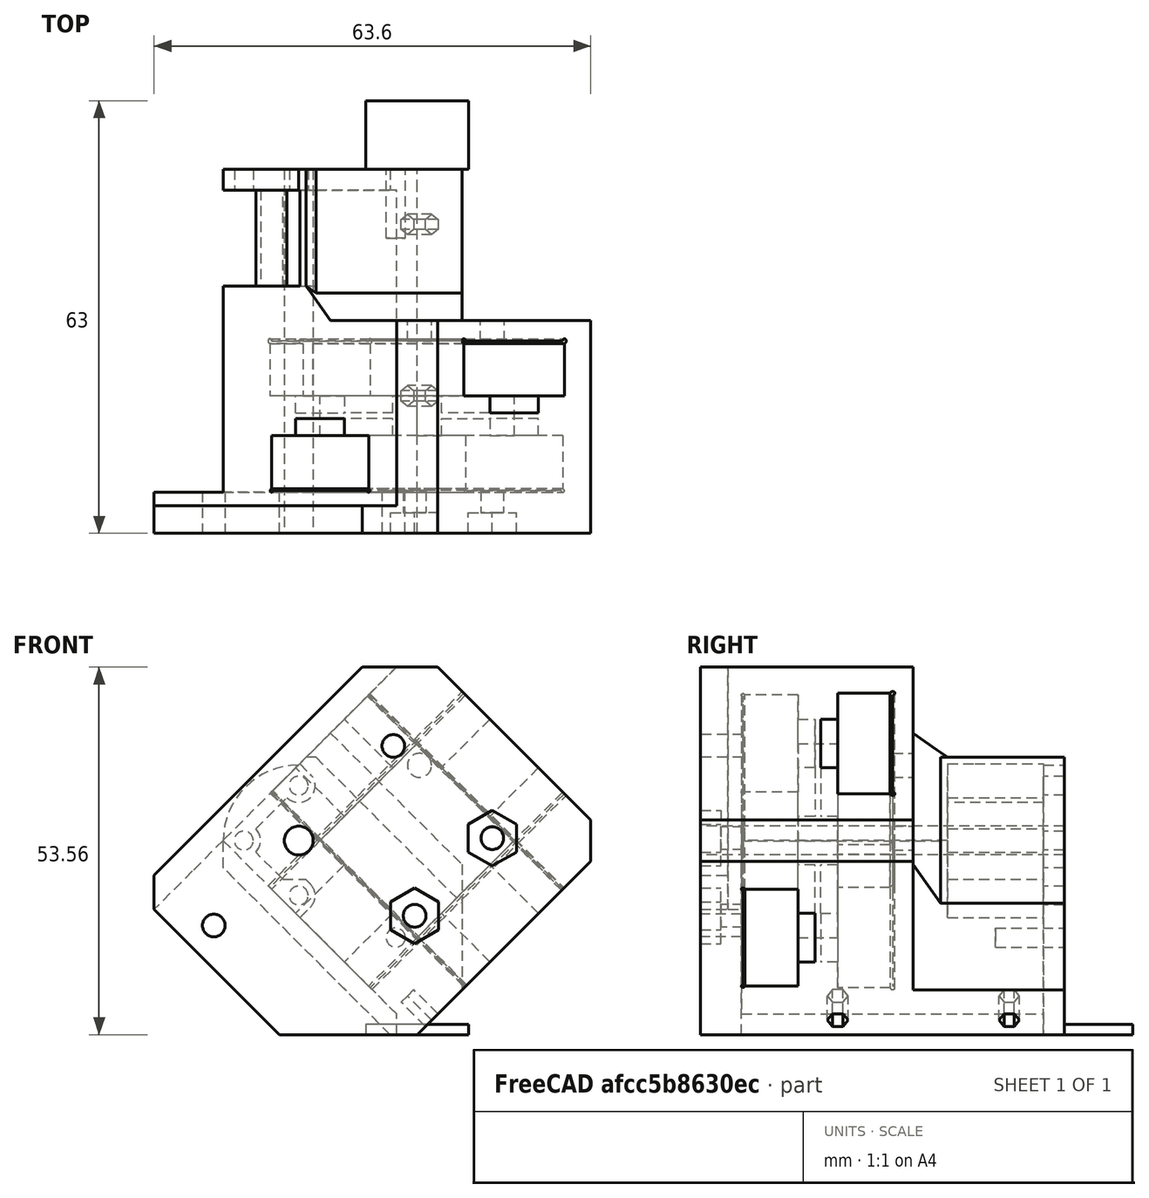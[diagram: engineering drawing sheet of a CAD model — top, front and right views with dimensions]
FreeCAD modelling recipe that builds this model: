
FCSTD DOCUMENT  (FreeCAD 0.19R)
Label: ToolHead_NoScreen
License: All rights reserved
LicenseURL: http://en.wikipedia.org/wiki/All_rights_reserved
objects: Sketcher::SketchObject×23, PartDesign::Pocket×14, PartDesign::Pad×5, PartDesign::Chamfer×2, PartDesign::Body×1
note: 66 computed .brp shape members not serialized (recipe doc carries the construction recipe); baked Part::Feature solids carry a one-line shape summary decoded from their .brp

FEATURE [Sketcher::SketchObject] Sketch  label="Body001"
  FullyConstrained = true
  MapMode = 5
  Support = -> [XY_Plane]
  sketch-geometry (11):
    g0: LineSegment StartX=20 StartY=15.7574 StartZ=0 EndX=20 EndY=-15.7574 EndZ=0
    g1: LineSegment StartX=15.7574 StartY=-20 StartZ=0 EndX=-20 EndY=-20 EndZ=0
    g2: LineSegment StartX=-20 StartY=-15.7574 StartZ=0 EndX=-20 EndY=19.9515 EndZ=0
    g3: Circle CenterX=-12.1976 CenterY=12.1976 CenterZ=0 NormalX=0 NormalY=0 NormalZ=1 AngleXU=0 Radius=2.1
    g4: LineSegment StartX=-12.1976 StartY=12.1976 StartZ=0 EndX=0 EndY=0 EndZ=0
    g5: ArcOfCircle CenterX=-12.1976 CenterY=12.1976 CenterZ=0 NormalX=0 NormalY=0 NormalZ=1 AngleXU=0 Radius=11 StartAngle=0.788519 EndAngle=2.35931
    g6: LineSegment StartX=-4.44373 StartY=20 StartZ=0 EndX=15.7574 EndY=20 EndZ=0
    g7: LineSegment StartX=15.7574 StartY=-20 StartZ=0 EndX=20 EndY=-15.7574 EndZ=0
    g8: LineSegment StartX=-20 StartY=-15.7574 StartZ=0 EndX=-22.1213 EndY=-17.8787 EndZ=0
    g9: LineSegment StartX=-22.1213 StartY=-17.8787 StartZ=0 EndX=-20 EndY=-20 EndZ=0
    g10: LineSegment StartX=15.7574 StartY=20 StartZ=0 EndX=20 EndY=15.7574 EndZ=0
  constraints (32):
    c: Horizontal(g1)
    c: Vertical(g0)
    c: Vertical(g2)
    c: Distance(g-1,g3) = 17.25
    c: Coincident(g4,g3)
    c: Coincident(g4,g-1)
    c: Angle(g4) = -0.785398
    c: Diameter(g3) = 4.2
    c: Coincident(g5,g3)
    c: Diameter(g5) = 22
    c: DistanceX(g1) = -20
    c: Coincident(g6,g5)
    c: Horizontal(g6)
    c: Coincident(g5,g2)
    c: Coincident(g7,g1)
    c: Coincident(g7,g0)
    c: Angle(g7) = 0.785398
    c: Distance(g7) = 6
    c: DistanceY(g1) = -20
    c: Coincident(g2,g8)
    c: Coincident(g8,g9)
    c: Coincident(g9,g1)
    c: Angle(g9) = -0.785398
    c: Angle(g8) = -2.35619
    c: Distance(g9) = 3
    c: DistanceX(g2) = -20
    c: Coincident(g10,g6)
    c: Coincident(g10,g0)
    c: Distance(g10) = 6
    c: Angle(g10) = -0.785398
    c: DistanceX(g0) = 20
    c: DistanceY(g6) = 20
FEATURE [PartDesign::Pad] Pad
  Direction = (1,1,1)
  Length = 53
  Length2 = 10
  Profile = -> Sketch
  Reversed = true
  Type = 0
FEATURE [Sketcher::SketchObject] Sketch001  label="RailHole"
  FullyConstrained = true
  MapMode = 5
  Placement = pos=(20,0,0) rot=(0.57735,0.57735,0.57735;2.0944rad)
  Support = -> [Pad]
  sketch-geometry (10):
    g0: LineSegment StartX=-10.35 StartY=-27.65 StartZ=0 EndX=-10.35 EndY=-20 EndZ=0
    g1: LineSegment StartX=5 StartY=-17.5 StartZ=0 EndX=-5 EndY=-17.5 EndZ=0
    g2: LineSegment StartX=10 StartY=-28 StartZ=0 EndX=-10 EndY=-28 EndZ=0
    g3: LineSegment StartX=5 StartY=-17.5 StartZ=0 EndX=5 EndY=-20 EndZ=0
    g4: LineSegment StartX=-5 StartY=-20 StartZ=0 EndX=-5 EndY=-17.5 EndZ=0
    g5: LineSegment StartX=-10.35 StartY=-20 StartZ=0 EndX=-5 EndY=-20 EndZ=0
    g6: LineSegment StartX=5 StartY=-20 StartZ=0 EndX=10.3495 EndY=-20 EndZ=0
    g7: LineSegment StartX=10.3495 StartY=-27.65 StartZ=0 EndX=10.3495 EndY=-20 EndZ=0
    g8: ArcOfCircle CenterX=-10.35 CenterY=-28 CenterZ=0 NormalX=0 NormalY=0 NormalZ=1 AngleXU=0 Radius=0.35 StartAngle=1.5708 EndAngle=6.28319
    g9: ArcOfCircle CenterX=10.35 CenterY=-28 CenterZ=0 NormalX=0 NormalY=0 NormalZ=1 AngleXU=0 Radius=0.35 StartAngle=3.14159 EndAngle=7.85541
  constraints (29):
    c: Vertical(g0)
    c: Symmetric(g1,g1,g-2)
    c: Distance(g1) = 10
    c: Coincident(g1,g3)
    c: Vertical(g3)
    c: Coincident(g4,g1)
    c: Symmetric(g3,g4,g-2)
    c: Distance(g3) = 2.5
    c: Distance(g2) = 20
    c: Coincident(g5,g4)
    c: Horizontal(g5)
    c: Coincident(g3,g6)
    c: Horizontal(g6)
    c: Vertical(g7)
    c: Coincident(g0,g5)
    c: Coincident(g7,g6)
    c: Coincident(g0,g8)
    c: Coincident(g8,g2)
    c: Diameter(g8) = 0.7
    c: DistanceX(g0,g8) = 0
    c: DistanceY(g2,g8) = 0
    c: Coincident(g9,g2)
    c: Coincident(g9,g7)
    c: Diameter(g9) = 0.7
    c: DistanceY(g2,g9) = 0
    c: DistanceX(g7,g9) = 0.0005
    c: Symmetric(g9,g8,g-2)
    c: Distance(g9,g6) = 8
    c: DistanceY(g8) = -28
FEATURE [PartDesign::Pocket] Pocket
  BaseFeature = -> Pad
  Length = 5
  Length2 = 100
  Profile = -> Sketch001
  Type = 1
FEATURE [Sketcher::SketchObject] Sketch008  label="ExtruderHole"
  FullyConstrained = false
  MapMode = 5
  Placement = pos=(0,0,4) rot=(0,0,1;0rad)
  sketch-geometry (2):
    g0: LineSegment StartX=0 StartY=0 StartZ=0 EndX=-54.6242 EndY=54.6242 EndZ=0
    g1: Circle CenterX=-12.1976 CenterY=12.1976 CenterZ=0 NormalX=0 NormalY=0 NormalZ=1 AngleXU=0 Radius=2.1
  constraints (5):
    c: Coincident(g0,g-1)
    c: Angle(g0) = 2.35619
    c: PointOnObject(g1,g0)
    c: Distance(g-1,g1) = 17.25
    c: Diameter(g1) = 4.2
FEATURE [Sketcher::SketchObject] Sketch009  label="reference"
  FullyConstrained = false
  MapMode = 5
  Placement = pos=(0,0,-25) rot=(1,0,0;3.14159rad)
  sketch-geometry (2):
    g0: Circle CenterX=-12.0208 CenterY=-12.0208 CenterZ=0 NormalX=0 NormalY=0 NormalZ=1 AngleXU=0 Radius=10
    g1: LineSegment StartX=0 StartY=0 StartZ=0 EndX=-27.7674 EndY=-27.7674 EndZ=0
  constraints (5):
    c: Diameter(g0) = 20
    c: Coincident(g1,g-1)
    c: Angle(g1) = -2.35619
    c: PointOnObject(g0,g1)
    c: Distance(g0,g1) = 17
FEATURE [Sketcher::SketchObject] Sketch010  label="reference2"
  FullyConstrained = false
  MapMode = 5
  Placement = pos=(0,0,-37) rot=(1,0,0;3.14159rad)
  sketch-geometry (2):
    g0: Circle CenterX=-12.1976 CenterY=-12.1976 CenterZ=0 NormalX=0 NormalY=0 NormalZ=1 AngleXU=0 Radius=8
    g1: LineSegment StartX=0 StartY=0 StartZ=0 EndX=-38.1566 EndY=-38.1566 EndZ=0
  constraints (5):
    c: Diameter(g0) = 16
    c: Coincident(g1,g-1)
    c: Angle(g1) = -2.35619
    c: Distance(g0,g1) = 17.25
    c: PointOnObject(g0,g1)
FEATURE [Sketcher::SketchObject] Sketch021  label="InternalTri"
  FullyConstrained = true
  MapMode = 5
  Placement = pos=(0,-3e-15,-12) rot=(0,0,1;0rad)
  sketch-geometry (4):
    g0: LineSegment StartX=-10 StartY=10 StartZ=0 EndX=10 EndY=10 EndZ=0
    g1: LineSegment StartX=10 StartY=10 StartZ=0 EndX=10 EndY=-10 EndZ=0
    g2: LineSegment StartX=10 StartY=-10 StartZ=0 EndX=-10 EndY=-10 EndZ=0
    g3: LineSegment StartX=-10 StartY=-10 StartZ=0 EndX=-10 EndY=10 EndZ=0
  constraints (11):
    c: Coincident(g0,g1)
    c: Coincident(g1,g2)
    c: Coincident(g2,g3)
    c: Coincident(g3,g0)
    c: Horizontal(g0)
    c: Horizontal(g2)
    c: Vertical(g1)
    c: Vertical(g3)
    c: Symmetric(g1,g0,g-1)
    c: Equal(g1,g0)
    c: Distance(g1) = 20
FEATURE [PartDesign::Pocket] Pocket002
  BaseFeature = -> Pocket
  Length = 10
  Length2 = 2
  Profile = -> Sketch021
  Type = 4
FEATURE [Sketcher::SketchObject] Sketch019  label="RailHole2"
  FullyConstrained = true
  MapMode = 5
  Placement = pos=(0,-20,0) rot=(1,0,0;1.5708rad)
  Support = -> [Pocket002]
  sketch-geometry (10):
    g0: LineSegment StartX=-9.75 StartY=-6.2 StartZ=0 EndX=9.75 EndY=-6.2 EndZ=0
    g1: LineSegment StartX=10 StartY=-14.2 StartZ=0 EndX=5 EndY=-14.2 EndZ=0
    g2: LineSegment StartX=5 StartY=-14.2 StartZ=0 EndX=5 EndY=-16.7 EndZ=0
    g3: LineSegment StartX=5 StartY=-16.7 StartZ=0 EndX=-5 EndY=-16.7 EndZ=0
    g4: LineSegment StartX=-5 StartY=-16.7 StartZ=0 EndX=-5 EndY=-14.2 EndZ=0
    g5: LineSegment StartX=-5 StartY=-14.2 StartZ=0 EndX=-10 EndY=-14.2 EndZ=0
    g6: ArcOfCircle CenterX=10 CenterY=-6.2 CenterZ=0 NormalX=0 NormalY=0 NormalZ=1 AngleXU=0 Radius=0.25 StartAngle=4.71239 EndAngle=9.42478
    g7: ArcOfCircle CenterX=-10 CenterY=-6.2 CenterZ=0 NormalX=0 NormalY=0 NormalZ=1 AngleXU=0 Radius=0.25 StartAngle=-9e-16 EndAngle=4.71239
    g8: LineSegment StartX=-10 StartY=-14.2 StartZ=0 EndX=-10 EndY=-6.45 EndZ=0
    g9: LineSegment StartX=10 StartY=-14.2 StartZ=0 EndX=10 EndY=-6.45 EndZ=0
  constraints (29):
    c: Horizontal(g0)
    c: Horizontal(g1)
    c: Coincident(g1,g2)
    c: Vertical(g2)
    c: Coincident(g2,g3)
    c: Horizontal(g3)
    c: Coincident(g3,g4)
    c: Vertical(g4)
    c: Coincident(g4,g5)
    c: Symmetric(g1,g5,g-2)
    c: Distance(g3) = 10
    c: Symmetric(g4,g1,g-2)
    c: DistanceY(g0) = -6.2
    c: Distance(g2) = 2.5
    c: Coincident(g6,g0)
    c: Coincident(g7,g0)
    c: Distance(g7,g6) = 20
    c: DistanceY(g1,g6) = 8
    c: Coincident(g8,g5)
    c: Vertical(g8)
    c: Coincident(g9,g1)
    c: Coincident(g9,g6)
    c: Vertical(g9)
    c: Coincident(g7,g8)
    c: Symmetric(g6,g7,g-2)
    c: Diameter(g6) = 0.5
    c: Equal(g6,g7)
    c: DistanceX(g7,g7) = 0
    c: DistanceY(g7,g0) = 0
FEATURE [Sketcher::SketchObject] Sketch024  label="hgxLITEholes"
  FullyConstrained = false
  MapMode = 5
  Placement = pos=(0,0,4) rot=(0,0,1;0rad)
  sketch-geometry (5):
    g0: Circle CenterX=7.30241 CenterY=12.1976 CenterZ=0 NormalX=0 NormalY=0 NormalZ=1 AngleXU=0 Radius=1.65
    g1: Circle CenterX=-29.6976 CenterY=12.1976 CenterZ=0 NormalX=0 NormalY=0 NormalZ=1 AngleXU=0 Radius=1.65
    g2: LineSegment StartX=-29.6976 StartY=12.1976 StartZ=0 EndX=7.30241 EndY=12.1976 EndZ=0
    g3: LineSegment StartX=0 StartY=0 StartZ=0 EndX=-27.1729 EndY=27.1729 EndZ=0
    g4: Circle CenterX=-12.1976 CenterY=12.1976 CenterZ=0 NormalX=0 NormalY=0 NormalZ=1 AngleXU=0 Radius=1.0154
  constraints (12):
    c: Diameter(g0) = 3.3
    c: Equal(g0,g1)
    c: Coincident(g2,g1)
    c: Coincident(g2,g0)
    c: Distance(g2) = 37
    c: Coincident(g3,g-1)
    c: Angle(g3) = 2.35619
    c: PointOnObject(g4,g3)
    c: Distance(g-1,g4) = 17.25
    c: Distance(g4,g0) = 19.5
    c: Horizontal(g2)
    c: PointOnObject(g4,g2)
FEATURE [PartDesign::Pocket] Pocket003
  BaseFeature = -> Pocket002
  Length = 5
  Length2 = 100
  Profile = -> Sketch019
  Type = 1
FEATURE [Sketcher::SketchObject] Sketch026  label="BottomSculp"
  FullyConstrained = false
  MapMode = 5
  Placement = pos=(0,0,-53) rot=(1,0,0;3.14159rad)
  Support = -> [Pocket003]
  sketch-geometry (5):
    g0: LineSegment StartX=29.4648 StartY=27.8981 StartZ=0 EndX=28.2209 EndY=-23.4245 EndZ=0
    g1: LineSegment StartX=28.2209 StartY=-23.4245 StartZ=0 EndX=-1.84855 EndY=-23.4245 EndZ=0
    g2: LineSegment StartX=-1.84855 StartY=-23.4245 StartZ=0 EndX=-1.84854 EndY=11.0762 EndZ=0
    g3: LineSegment StartX=-1.84854 StartY=11.0762 StartZ=0 EndX=-16.3575 EndY=25.5852 EndZ=0
    g4: LineSegment StartX=-16.3575 StartY=25.5852 StartZ=0 EndX=29.4648 EndY=27.8981 EndZ=0
  constraints (8):
    c: Coincident(g0,g1)
    c: Horizontal(g1)
    c: Coincident(g1,g2)
    c: Angle(g2) = 1.5708
    c: Coincident(g2,g3)
    c: Angle(g3) = 2.35619
    c: Coincident(g4,g3)
    c: Coincident(g4,g0)
FEATURE [PartDesign::Pocket] Pocket004
  BaseFeature = -> Pocket003
  Length = 22
  Length2 = 100
  Profile = -> Sketch026
  Type = 0
FEATURE [Sketcher::SketchObject] Sketch004  label="Yboltpattern"
  FullyConstrained = true
  MapMode = 5
  Placement = pos=(0,0,-31) rot=(1,0,0;3.14159rad)
  Support = -> [Pocket004]
  sketch-geometry (8):
    g0: Circle CenterX=-8 CenterY=7.5 CenterZ=0 NormalX=0 NormalY=0 NormalZ=1 AngleXU=0 Radius=1.75
    g1: Circle CenterX=8 CenterY=7.5 CenterZ=0 NormalX=0 NormalY=0 NormalZ=1 AngleXU=0 Radius=1.75
    g2: Circle CenterX=-8 CenterY=-7.5 CenterZ=0 NormalX=0 NormalY=0 NormalZ=1 AngleXU=0 Radius=1.75
    g3: Circle CenterX=8 CenterY=-7.5 CenterZ=0 NormalX=0 NormalY=0 NormalZ=1 AngleXU=0 Radius=1.75
    g4: LineSegment StartX=-8 StartY=7.5 StartZ=0 EndX=8 EndY=7.5 EndZ=0
    g5: LineSegment StartX=8 StartY=7.5 StartZ=0 EndX=8 EndY=-7.5 EndZ=0
    g6: LineSegment StartX=8 StartY=-7.5 StartZ=0 EndX=-8 EndY=-7.5 EndZ=0
    g7: LineSegment StartX=-8 StartY=-7.5 StartZ=0 EndX=-8 EndY=7.5 EndZ=0
  constraints (18):
    c: Diameter(g0) = 3.5
    c: Equal(g0,g1)
    c: Equal(g0,g2)
    c: Equal(g0,g3)
    c: Distance(g2,g0) = 15
    c: Distance(g3,g2) = 16
    c: Coincident(g4,g0)
    c: Coincident(g4,g1)
    c: Coincident(g4,g5)
    c: Coincident(g5,g3)
    c: Coincident(g5,g6)
    c: Coincident(g6,g2)
    c: Coincident(g6,g7)
    c: Coincident(g7,g4)
    c: Equal(g5,g7)
    c: Equal(g4,g6)
    c: Symmetric(g1,g2,g-1)
    c: Symmetric(g0,g1,g-2)
FEATURE [Sketcher::SketchObject] Sketch022  label="VoronHoleRelif"
  FullyConstrained = true
  MapMode = 5
  Placement = pos=(0,0,-28) rot=(0,0,1;0rad)
  Support = -> [Pocket004]
  sketch-geometry (11):
    g0: ArcOfCircle CenterX=-17.8884 CenterY=6.52425 CenterZ=0 NormalX=0 NormalY=0 NormalZ=1 AngleXU=0 Radius=2.4 StartAngle=4.71239 EndAngle=6.28319
    g1: ArcOfCircle CenterX=-6.58192 CenterY=17.8307 CenterZ=0 NormalX=0 NormalY=0 NormalZ=1 AngleXU=0 Radius=2.4 StartAngle=3.14159 EndAngle=6.28319
    g2: LineSegment StartX=-22.2684 StartY=4.12425 StartZ=0 EndX=-17.8884 EndY=4.12425 EndZ=0
    g3: LineSegment StartX=-22.2684 StartY=23.8307 StartZ=0 EndX=-4.18192 EndY=23.8307 EndZ=0
    g4: LineSegment StartX=-4.18192 StartY=23.8307 StartZ=0 EndX=-4.18192 EndY=17.8307 EndZ=0
    g5: LineSegment StartX=-22.2684 StartY=4.12425 StartZ=0 EndX=-22.2684 EndY=23.8307 EndZ=0
    g6: ArcOfCircle CenterX=-17.8172 CenterY=17.8307 CenterZ=0 NormalX=0 NormalY=0 NormalZ=1 AngleXU=0 Radius=2.4 StartAngle=4.71239 EndAngle=6.28319
    g7: LineSegment StartX=-15.4172 StartY=17.8307 StartZ=0 EndX=-8.98192 EndY=17.8307 EndZ=0
    g8: LineSegment StartX=-17.8172 StartY=9.85307 StartZ=0 EndX=-15.4884 EndY=7.52425 EndZ=0
    g9: LineSegment StartX=-15.4884 StartY=6.52425 StartZ=0 EndX=-15.4884 EndY=7.52425 EndZ=0
    g10: LineSegment StartX=-17.8172 StartY=9.85307 StartZ=0 EndX=-17.8172 EndY=15.4307 EndZ=0
  constraints (33):
    c: Horizontal(g2)
    c: Coincident(g3,g4)
    c: Tangent(g4,g1) = 1.5708
    c: Tangent(g2,g0) = -1.5708
    c: Diameter(g0) = 4.8
    c: Equal(g0,g1)
    c: Vertical(g4)
    c: Horizontal(g3)
    c: Coincident(g5,g2)
    c: Coincident(g5,g3)
    c: Vertical(g5)
    c: Distance(g2) = 4.38
    c: Distance(g4) = 6
    c: DistanceX(g1) = -6.58192
    c: DistanceY(g1) = 17.8307
    c: DistanceX(g0) = -17.8884
    c: DistanceY(g0) = 6.52425
    c: Coincident(g7,g6)
    c: Coincident(g7,g1)
    c: Horizontal(g7)
    c: Perpendicular(g1,g7)
    c: Diameter(g6) = 4.8
    c: Perpendicular(g6,g7)
    c: Angle(g8) = -0.785398
    c: Vertical(g9)
    c: Tangent(g9,g0) = -1.5708
    c: Distance(g9) = 1
    c: Coincident(g8,g9)
    c: Coincident(g10,g8)
    c: Coincident(g10,g6)
    c: Vertical(g10)
    c: Perpendicular(g6,g10)
    c: DistanceX(g6) = -17.8172
FEATURE [PartDesign::Pocket] Pocket005
  BaseFeature = -> Pocket004
  Length = 22
  Length2 = -8
  Profile = -> Sketch022
  Type = 4
FEATURE [Sketcher::SketchObject] Sketch017  label="VoronHoles3"
  FullyConstrained = true
  MapMode = 5
  Placement = pos=(0,0,-50) rot=(0,0,1;0rad)
  Support = -> [Pocket005]
  sketch-geometry (10):
    g0: Circle CenterX=-6.54074 CenterY=17.8544 CenterZ=0 NormalX=0 NormalY=0 NormalZ=1 AngleXU=0 Radius=1.375
    g1: Circle CenterX=-17.8544 CenterY=6.54074 CenterZ=0 NormalX=0 NormalY=0 NormalZ=1 AngleXU=0 Radius=1.375
    g2: Circle CenterX=-6.54074 CenterY=6.54074 CenterZ=0 NormalX=0 NormalY=0 NormalZ=1 AngleXU=0 Radius=1.375
    g3: Circle CenterX=-17.8544 CenterY=17.8544 CenterZ=0 NormalX=0 NormalY=0 NormalZ=1 AngleXU=0 Radius=1.375
    g4: LineSegment StartX=-6.54074 StartY=17.8544 StartZ=0 EndX=-6.54074 EndY=6.54074 EndZ=0
    g5: LineSegment StartX=-6.54074 StartY=6.54074 StartZ=0 EndX=-17.8544 EndY=6.54074 EndZ=0
    g6: LineSegment StartX=-17.8544 StartY=6.54074 StartZ=0 EndX=-17.8544 EndY=17.8544 EndZ=0
    g7: LineSegment StartX=-17.8544 StartY=17.8544 StartZ=0 EndX=-6.54074 EndY=17.8544 EndZ=0
    g8: LineSegment StartX=0 StartY=0 StartZ=0 EndX=-37.1726 EndY=37.1726 EndZ=0
    g9: Circle CenterX=-12.1976 CenterY=12.1976 CenterZ=0 NormalX=0 NormalY=0 NormalZ=1 AngleXU=0 Radius=0.77
  constraints (25):
    c: Coincident(g4,g0)
    c: Coincident(g4,g2)
    c: Coincident(g4,g5)
    c: Coincident(g5,g1)
    c: Coincident(g5,g6)
    c: Coincident(g6,g3)
    c: Coincident(g6,g7)
    c: Coincident(g7,g4)
    c: Equal(g4,g7)
    c: Equal(g7,g6)
    c: Equal(g6,g5)
    c: Coincident(g8,g-1)
    c: PointOnObject(g9,g8)
    c: Distance(g-1,g9) = 17.25
    c: Diameter(g1) = 2.75
    c: Equal(g1,g3)
    c: Equal(g1,g0)
    c: Equal(g1,g2)
    c: Symmetric(g0,g1,g9)
    c: Distance(g2,g3) = 16
    c: Angle(g8) = 2.35619
    c: PointOnObject(g2,g8)
    c: Perpendicular(g7,g4)
    c: Distance(g8) = 52.57
    c: Diameter(g9) = 1.54
FEATURE [PartDesign::Pocket] Pocket006
  BaseFeature = -> Pocket005
  Length = 5
  Length2 = 100
  Profile = -> Sketch017
  Type = 1
FEATURE [Sketcher::SketchObject] Sketch025  label="FanDuctMountHole"
  FullyConstrained = true
  MapMode = 5
  Placement = pos=(0,0,-53) rot=(1,0,0;3.14159rad)
  Support = -> [Pocket006]
  sketch-geometry (1):
    g0: Circle CenterX=-12.2 CenterY=7.8 CenterZ=0 NormalX=0 NormalY=0 NormalZ=1 AngleXU=0 Radius=1.4
  constraints (3):
    c: Diameter(g0) = 2.8
    c: DistanceX(g0) = -12.2
    c: DistanceY(g0) = 7.8
FEATURE [PartDesign::Pocket] Pocket007
  BaseFeature = -> Pocket006
  Length = 10
  Length2 = 100
  Profile = -> Sketch025
  Type = 0
FEATURE [PartDesign::Pocket] Pocket008
  BaseFeature = -> Pocket007
  Length = 9
  Length2 = 100
  Profile = -> Sketch004
  Type = 0
FEATURE [Sketcher::SketchObject] Sketch007  label="ExtruderPlatform"
  ExternalGeometry = -> [Pad]
  FullyConstrained = false
  MapMode = 5
  Support = -> [Pocket008]
  sketch-geometry (12):
    g0: LineSegment StartX=-20 StartY=-20 StartZ=0 EndX=15.7574 EndY=-20 EndZ=0
    g1: LineSegment StartX=0 StartY=0 StartZ=0 EndX=-70.7107 EndY=70.7107 EndZ=0
    g2: Circle CenterX=-12.1976 CenterY=12.1976 CenterZ=0 NormalX=0 NormalY=0 NormalZ=1 AngleXU=0 Radius=2.125
    g3: LineSegment StartX=15.7574 StartY=-20 StartZ=0 EndX=20 EndY=-15.7574 EndZ=0
    g4: LineSegment StartX=20 StartY=-15.7574 StartZ=0 EndX=20 EndY=15.7574 EndZ=0
    g5: LineSegment StartX=20 StartY=15.7574 StartZ=0 EndX=15.7574 EndY=20 EndZ=0
    g6: LineSegment StartX=-20 StartY=-20 StartZ=0 EndX=-34.1976 EndY=-5.80241 EndZ=0
    g7: LineSegment StartX=-12.1976 StartY=-100 StartZ=0 EndX=-12.1976 EndY=100 EndZ=0
    g8: LineSegment StartX=-34.1976 StartY=-5.80241 StartZ=0 EndX=-34.1976 EndY=20 EndZ=0
    g9: LineSegment StartX=-34.1976 StartY=20 StartZ=0 EndX=15.7574 EndY=20 EndZ=0
    g10: Circle CenterX=-29.6976 CenterY=12.1976 CenterZ=0 NormalX=0 NormalY=0 NormalZ=1 AngleXU=0 Radius=1.4
    g11: Circle CenterX=7.30241 CenterY=11.9057 CenterZ=0 NormalX=0 NormalY=0 NormalZ=1 AngleXU=0 Radius=1.4
  constraints (35):
    c: Coincident(g1,g-1)
    c: Angle(g1) = 2.35619
    c: Diameter(g2) = 4.25
    c: PointOnObject(g2,g1)
    c: Distance(g-1,g2) = 17.25
    c: Coincident(g0,g3)
    c: Coincident(g3,g4)
    c: Coincident(g6,g0)
    c: Angle(g6) = 2.35619
    c: Coincident(g5,g4)
    c: Distance(g1) = 100
    c: PointOnObject(g2,g7)
    c: DistanceX(g0,g0) = -35.7574
    c: DistanceY(g0,g0) = 0
    c: DistanceX(g3,g0) = -40
    c: DistanceY(g3,g0) = -4.24264
    c: DistanceX(g4) = 20
    c: DistanceY(g4) = 15.7574
    c: DistanceX(g3) = 20
    c: DistanceY(g3) = -15.7574
    c: Coincident(g8,g6)
    c: Vertical(g8)
    c: Horizontal(g9)
    c: Coincident(g5,g9)
    c: Distance(g8,g7) = 22
    c: DistanceX(g5) = 15.7574
    c: DistanceY(g5) = 20
    c: Symmetric(g7,g7,g-1)
    c: Distance(g7) = 200
    c: DistanceX(g10,g2) = 17.5
    c: DistanceX(g2,g11) = 19.5
    c: Diameter(g10) = 2.8
    c: Equal(g10,g11)
    c: DistanceY(g10,g2) = 0
    c: Coincident(g9,g8)
FEATURE [PartDesign::Pad] Pad001
  BaseFeature = -> Pocket008
  Direction = (1,1,1)
  Length = 6
  Length2 = 100
  Profile = -> Sketch007
  Reversed = true
  Type = 0
FEATURE [PartDesign::Pocket] Pocket009
  BaseFeature = -> Pad001
  Length = 11
  Length2 = 100
  Profile = -> Sketch024
  Type = 0
FEATURE [PartDesign::Pocket] Pocket010
  BaseFeature = -> Pocket009
  Length = 5
  Length2 = 100
  Profile = -> Sketch008
  Type = 1
FEATURE [Sketcher::SketchObject] Sketch003  label="Xboltpattern"
  FullyConstrained = true
  MapMode = 5
  Support = -> [Pocket010]
  sketch-geometry (8):
    g0: Circle CenterX=-8 CenterY=7.5 CenterZ=0 NormalX=0 NormalY=0 NormalZ=1 AngleXU=0 Radius=1.65
    g1: Circle CenterX=8 CenterY=7.5 CenterZ=0 NormalX=0 NormalY=0 NormalZ=1 AngleXU=0 Radius=1.65
    g2: Circle CenterX=-8 CenterY=-7.5 CenterZ=0 NormalX=0 NormalY=0 NormalZ=1 AngleXU=0 Radius=1.65
    g3: Circle CenterX=8 CenterY=-7.5 CenterZ=0 NormalX=0 NormalY=0 NormalZ=1 AngleXU=0 Radius=1.65
    g4: LineSegment StartX=-8 StartY=7.5 StartZ=0 EndX=8 EndY=7.5 EndZ=0
    g5: LineSegment StartX=8 StartY=7.5 StartZ=0 EndX=8 EndY=-7.5 EndZ=0
    g6: LineSegment StartX=8 StartY=-7.5 StartZ=0 EndX=-8 EndY=-7.5 EndZ=0
    g7: LineSegment StartX=-8 StartY=-7.5 StartZ=0 EndX=-8 EndY=7.5 EndZ=0
  constraints (19):
    c: Diameter(g0) = 3.3
    c: Equal(g0,g1)
    c: Equal(g0,g2)
    c: Equal(g0,g3)
    c: Distance(g0,g1) = 16
    c: Distance(g1,g3) = 15
    c: Coincident(g4,g0)
    c: Coincident(g4,g1)
    c: Horizontal(g4)
    c: Coincident(g4,g5)
    c: Coincident(g5,g3)
    c: Vertical(g5)
    c: Coincident(g5,g6)
    c: Coincident(g6,g2)
    c: Coincident(g6,g7)
    c: Coincident(g7,g4)
    c: Symmetric(g2,g1,g-1)
    c: Equal(g7,g5)
    c: Equal(g6,g4)
FEATURE [Sketcher::SketchObject] Sketch029  label="Adhesion"
  FullyConstrained = false
  MapMode = 5
  Placement = pos=(0,0,-53) rot=(1,0,0;3.14159rad)
  sketch-geometry (4):
    g0: LineSegment StartX=-13.636 StartY=24.2426 StartZ=0 EndX=-24.2426 EndY=13.636 EndZ=0
    g1: LineSegment StartX=-24.2426 StartY=13.636 StartZ=0 EndX=-25.3033 EndY=14.6967 EndZ=0
    g2: LineSegment StartX=-25.3033 StartY=14.6967 StartZ=0 EndX=-14.6967 EndY=25.3033 EndZ=0
    g3: LineSegment StartX=-14.6967 StartY=25.3033 StartZ=0 EndX=-13.636 EndY=24.2426 EndZ=0
  constraints (10):
    c: Coincident(g0,g1)
    c: Coincident(g1,g2)
    c: Coincident(g2,g3)
    c: Coincident(g3,g0)
    c: Angle(g2) = 0.785398
    c: Distance(g2) = 15
    c: Distance(g1) = 1.5
    c: Distance(g3) = 1.5
    c: Perpendicular(g2,g3)
    c: Perpendicular(g2,g1)
FEATURE [Sketcher::SketchObject] Sketch033  label="WireMgmnt"
  FullyConstrained = true
  MapMode = 5
  Placement = pos=(0,-20,0) rot=(1,0,0;1.5708rad)
  sketch-geometry (14):
    g0: LineSegment StartX=-15.7 StartY=-20.7506 StartZ=0 EndX=-15.7 EndY=-19.2494 EndZ=0
    g1: LineSegment StartX=-15.7 StartY=-19.2494 StartZ=0 EndX=-17 EndY=-18.4989 EndZ=0
    g2: LineSegment StartX=-17 StartY=-18.4989 StartZ=0 EndX=-18.3 EndY=-19.2494 EndZ=0
    g3: LineSegment StartX=-18.3 StartY=-19.2494 StartZ=0 EndX=-18.3 EndY=-20.7506 EndZ=0
    g4: LineSegment StartX=-18.3 StartY=-20.7506 StartZ=0 EndX=-17 EndY=-21.5011 EndZ=0
    g5: LineSegment StartX=-17 StartY=-21.5011 StartZ=0 EndX=-15.7 EndY=-20.7506 EndZ=0
    g6: Circle CenterX=-17 CenterY=-20 CenterZ=0 NormalX=0 NormalY=0 NormalZ=1 AngleXU=0 Radius=1.50111
    g7: LineSegment StartX=-15.7 StartY=-44.2494 StartZ=0 EndX=-17 EndY=-43.4989 EndZ=0
    g8: LineSegment StartX=-17 StartY=-43.4989 StartZ=0 EndX=-18.3 EndY=-44.2494 EndZ=0
    g9: LineSegment StartX=-18.3 StartY=-44.2494 StartZ=0 EndX=-18.3 EndY=-45.7506 EndZ=0
    g10: LineSegment StartX=-18.3 StartY=-45.7506 StartZ=0 EndX=-17 EndY=-46.5011 EndZ=0
    g11: LineSegment StartX=-17 StartY=-46.5011 StartZ=0 EndX=-15.7 EndY=-45.7506 EndZ=0
    g12: LineSegment StartX=-15.7 StartY=-45.7506 StartZ=0 EndX=-15.7 EndY=-44.2494 EndZ=0
    g13: Circle CenterX=-17 CenterY=-45 CenterZ=0 NormalX=0 NormalY=0 NormalZ=1 AngleXU=0 Radius=1.50111
  constraints (34):
    c: Coincident(g0,g1)
    c: Coincident(g1,g2)
    c: Coincident(g2,g3)
    c: Coincident(g3,g4)
    c: Coincident(g4,g5)
    c: Coincident(g5,g0)
    c: Equal(g0, g1-g5) x5
    c: PointOnObject(g0,g6)
    c: PointOnObject(g1,g6)
    c: PointOnObject(g2,g6)
    c: PointOnObject(g3,g6)
    c: PointOnObject(g4,g6)
    c: PointOnObject(g5,g6)
    c: Coincident(g7,g8)
    c: Coincident(g8,g9)
    c: Coincident(g9,g10)
    c: Coincident(g10,g11)
    c: Coincident(g11,g12)
    c: Coincident(g12,g7)
    c: Equal(g7, g8-g12) x5
    c: PointOnObject(g7,g13)
    c: PointOnObject(g8,g13)
    c: PointOnObject(g9,g13)
    c: PointOnObject(g10,g13)
    c: PointOnObject(g11,g13)
    c: PointOnObject(g12,g13)
    c: DistanceX(g13) = -17
    c: Distance(g10,g7) = 2.6
    c: Vertical(g9)
    c: DistanceY(g13) = -45
    c: Distance(g3,g0) = 2.6
    c: DistanceY(g6) = -20
    c: Vertical(g3)
    c: DistanceX(g6) = -17
FEATURE [Sketcher::SketchObject] Sketch035  label="Bottom Reinforce"
  FullyConstrained = false
  MapMode = 5
  Placement = pos=(0,0,-53) rot=(1,0,0;3.14159rad)
  sketch-geometry (4):
    g0: LineSegment StartX=-22.779 StartY=17.221 StartZ=0 EndX=-22.779 EndY=-17.1725 EndZ=0
    g1: LineSegment StartX=-22.779 StartY=-17.1725 StartZ=0 EndX=-20 EndY=-19.9515 EndZ=0
    g2: LineSegment StartX=-20 StartY=-19.9515 StartZ=0 EndX=-20 EndY=20 EndZ=0
    g3: LineSegment StartX=-20 StartY=20 StartZ=0 EndX=-22.779 EndY=17.221 EndZ=0
  constraints (9):
    c: Vertical(g0)
    c: Coincident(g0,g1)
    c: Coincident(g1,g2)
    c: Vertical(g2)
    c: Coincident(g2,g3)
    c: Coincident(g3,g0)
    c: Angle(g1) = -0.785398
    c: DistanceY(g2) = 20
    c: Angle(g3) = -2.35619
FEATURE [Sketcher::SketchObject] Sketch037
  FullyConstrained = false
  MapMode = 5
  sketch-geometry (4):
    g0: LineSegment StartX=-26.2848 StartY=31.2083 StartZ=0 EndX=-1.26106 EndY=31.2083 EndZ=0
    g1: LineSegment StartX=-1.26106 StartY=31.2083 StartZ=0 EndX=-1.26106 EndY=20 EndZ=0
    g2: LineSegment StartX=-1.26106 StartY=20 StartZ=0 EndX=-26.2848 EndY=20 EndZ=0
    g3: LineSegment StartX=-26.2848 StartY=20 StartZ=0 EndX=-26.2848 EndY=31.2083 EndZ=0
  constraints (9):
    c: Coincident(g0,g1)
    c: Coincident(g1,g2)
    c: Coincident(g2,g3)
    c: Coincident(g3,g0)
    c: Horizontal(g0)
    c: Horizontal(g2)
    c: Vertical(g1)
    c: Vertical(g3)
    c: DistanceY(g1) = 20
FEATURE [PartDesign::Pocket] Pocket011
  BaseFeature = -> Pocket010
  Length = 10
  Length2 = 100
  Profile = -> Sketch003
  Type = 0
FEATURE [Sketcher::SketchObject] Sketch036  label="countersink"
  FullyConstrained = true
  MapMode = 5
  Support = -> [Pocket011]
  sketch-geometry (14):
    g0: LineSegment StartX=11.9037 StartY=-8.546 StartZ=0 EndX=10.8577 EndY=-4.64226 EndZ=0
    g1: LineSegment StartX=10.8577 StartY=-4.64226 StartZ=0 EndX=6.954 EndY=-3.59626 EndZ=0
    g2: LineSegment StartX=6.954 StartY=-3.59626 StartZ=0 EndX=4.09626 EndY=-6.454 EndZ=0
    g3: LineSegment StartX=4.09626 StartY=-6.454 StartZ=0 EndX=5.14226 EndY=-10.3577 EndZ=0
    g4: LineSegment StartX=5.14226 StartY=-10.3577 StartZ=0 EndX=9.046 EndY=-11.4037 EndZ=0
    g5: LineSegment StartX=9.046 StartY=-11.4037 StartZ=0 EndX=11.9037 EndY=-8.546 EndZ=0
    g6: Circle CenterX=8 CenterY=-7.5 CenterZ=0 NormalX=0 NormalY=0 NormalZ=1 AngleXU=0 Radius=4.04145
    g7: LineSegment StartX=-5.14226 StartY=-4.64226 StartZ=0 EndX=-9.046 EndY=-3.59626 EndZ=0
    g8: LineSegment StartX=-9.046 StartY=-3.59626 StartZ=0 EndX=-11.9037 EndY=-6.454 EndZ=0
    g9: LineSegment StartX=-11.9037 StartY=-6.454 StartZ=0 EndX=-10.8577 EndY=-10.3577 EndZ=0
    g10: LineSegment StartX=-10.8577 StartY=-10.3577 StartZ=0 EndX=-6.954 EndY=-11.4037 EndZ=0
    g11: LineSegment StartX=-6.954 StartY=-11.4037 StartZ=0 EndX=-4.09626 EndY=-8.546 EndZ=0
    g12: LineSegment StartX=-4.09626 StartY=-8.546 StartZ=0 EndX=-5.14226 EndY=-4.64226 EndZ=0
    g13: Circle CenterX=-8 CenterY=-7.5 CenterZ=0 NormalX=0 NormalY=0 NormalZ=1 AngleXU=0 Radius=4.04145
  constraints (34):
    c: Coincident(g0,g1)
    c: Coincident(g1,g2)
    c: Coincident(g2,g3)
    c: Coincident(g3,g4)
    c: Coincident(g4,g5)
    c: Coincident(g5,g0)
    c: Equal(g0, g1-g5) x5
    c: PointOnObject(g0,g6)
    c: PointOnObject(g1,g6)
    c: PointOnObject(g2,g6)
    c: PointOnObject(g3,g6)
    c: PointOnObject(g4,g6)
    c: PointOnObject(g5,g6)
    c: Coincident(g7,g8)
    c: Coincident(g8,g9)
    c: Coincident(g9,g10)
    c: Coincident(g10,g11)
    c: Coincident(g11,g12)
    c: Coincident(g12,g7)
    c: Equal(g7, g8-g12) x5
    c: PointOnObject(g7,g13)
    c: PointOnObject(g8,g13)
    c: PointOnObject(g9,g13)
    c: PointOnObject(g10,g13)
    c: PointOnObject(g11,g13)
    c: PointOnObject(g12,g13)
    c: Angle(g11) = 0.785398
    c: Angle(g5) = 0.785398
    c: Distance(g0,g2) = 7
    c: Distance(g7,g8) = 7
    c: DistanceX(g6) = 8
    c: DistanceY(g6) = -7.5
    c: DistanceY(g13) = -7.5
    c: DistanceX(g13) = -8
FEATURE [PartDesign::Pocket] Pocket012
  BaseFeature = -> Pocket011
  Length = 3
  Length2 = 100
  Profile = -> Sketch036
  Type = 0
FEATURE [PartDesign::Pocket] Pocket013
  BaseFeature = -> Pocket012
  Length = 5
  Length2 = 100
  Profile = -> Sketch033
  Type = 0
FEATURE [PartDesign::Pad] Pad002
  BaseFeature = -> Pocket013
  Direction = (1,1,1)
  Length = 3
  Length2 = 100
  Profile = -> Sketch035
  Reversed = true
  Type = 0
FEATURE [PartDesign::Pocket] Pocket014
  BaseFeature = -> Pad002
  Length = 40
  Length2 = 100
  Profile = -> Sketch037
  Type = 0
FEATURE [PartDesign::Pad] Pad003
  BaseFeature = -> Pocket014
  Direction = (1,1,1)
  Length = 10
  Length2 = 100
  Profile = -> Sketch029
  Type = 0
FEATURE [Sketcher::SketchObject] Sketch038
  FullyConstrained = true
  MapMode = 5
  Placement = pos=(0,20,0) rot=(0,0.707107,0.707107;3.14159rad)
  Support = -> [Pad003]
FEATURE [Sketcher::SketchObject] Sketch039
  ExternalGeometry = -> [Pad003]
  FullyConstrained = true
  MapMode = 5
  Support = -> [Pad003]
  sketch-geometry (4):
    g0: LineSegment StartX=-30.6621 StartY=23.5355 StartZ=0 EndX=12.2218 EndY=23.5355 EndZ=0
    g1: LineSegment StartX=12.2218 StartY=23.5355 StartZ=0 EndX=15.7574 EndY=20 EndZ=0
    g2: LineSegment StartX=15.7574 StartY=20 StartZ=0 EndX=-34.1976 EndY=20 EndZ=0
    g3: LineSegment StartX=-34.1976 StartY=20 StartZ=0 EndX=-30.6621 EndY=23.5355 EndZ=0
  constraints (10):
    c: Coincident(g0,g1)
    c: Coincident(g1,g2)
    c: Coincident(g2,g3)
    c: Coincident(g3,g0)
    c: Horizontal(g0)
    c: Distance(g1) = 5
    c: Coincident(g2,g-3)
    c: Coincident(g1,g-4)
    c: Angle(g1) = -0.785398
    c: Angle(g3) = 0.785398
FEATURE [PartDesign::Pad] Pad004
  BaseFeature = -> Pad003
  Direction = (1,1,1)
  Length = 4
  Length2 = 100
  Profile = -> Sketch039
  Reversed = true
  Type = 0
FEATURE [PartDesign::Chamfer] Chamfer
  Angle = 45
  Base = -> Pad004 [Edge142]
  BaseFeature = -> Pad004
  ChamferType = 0
  FlipDirection = false
  Size = 4
  Size2 = 1
  SupportTransform = false
FEATURE [PartDesign::Chamfer] Chamfer001
  Angle = 45
  Base = -> Chamfer [Edge99]
  BaseFeature = -> Chamfer
  ChamferType = 0
  FlipDirection = false
  Size = 1
  Size2 = 1
  SupportTransform = false
FEATURE [Sketcher::SketchObject] Sketch040
  FullyConstrained = false
  MapMode = 5
  Placement = pos=(17.8787,-17.8787,0) rot=(0.862856,0.357407,0.357407;1.71777rad)
  Support = -> [Chamfer001]
  sketch-geometry (16):
    g0: LineSegment StartX=-41.3399 StartY=8.3544 StartZ=0 EndX=41.3856 EndY=8.3544 EndZ=0
    g1: LineSegment StartX=41.3856 StartY=8.3544 StartZ=0 EndX=41.3856 EndY=-10 EndZ=0
    g2: LineSegment StartX=41.3856 StartY=-10 StartZ=0 EndX=-41.3399 EndY=-10 EndZ=0
    g3: LineSegment StartX=-41.3399 StartY=-10 StartZ=0 EndX=-41.3399 EndY=8.3544 EndZ=0
    g4: LineSegment StartX=-40.7799 StartY=-25 StartZ=0 EndX=41.91 EndY=-25 EndZ=0
    g5: LineSegment StartX=41.91 StartY=-25 StartZ=0 EndX=41.91 EndY=-68.8503 EndZ=0
    g6: LineSegment StartX=41.91 StartY=-68.8503 StartZ=0 EndX=-40.7799 EndY=-68.8503 EndZ=0
    g7: LineSegment StartX=-40.7799 StartY=-68.8503 StartZ=0 EndX=-40.7799 EndY=-25 EndZ=0
    g8: LineSegment StartX=-35 StartY=-24 StartZ=0 EndX=-35 EndY=-11 EndZ=0
    g9: LineSegment StartX=-35 StartY=-11 StartZ=0 EndX=60 EndY=-11 EndZ=0
    g10: LineSegment StartX=60 StartY=-24 StartZ=0 EndX=-35 EndY=-24 EndZ=0
    g11: LineSegment StartX=60 StartY=-24 StartZ=0 EndX=60 EndY=-75 EndZ=0
    g12: LineSegment StartX=60 StartY=-75 StartZ=0 EndX=-60 EndY=-75 EndZ=0
    g13: LineSegment StartX=-60 StartY=-75 StartZ=0 EndX=-60 EndY=20 EndZ=0
    g14: LineSegment StartX=-60 StartY=20 StartZ=0 EndX=60 EndY=20 EndZ=0
    g15: LineSegment StartX=60 StartY=20 StartZ=0 EndX=60 EndY=-11 EndZ=0
  constraints (40):
    c: Coincident(g0,g1)
    c: Coincident(g1,g2)
    c: Coincident(g2,g3)
    c: Coincident(g3,g0)
    c: Horizontal(g0)
    c: Horizontal(g2)
    c: Vertical(g1)
    c: Vertical(g3)
    c: DistanceY(g1) = -10
    c: Coincident(g4,g5)
    c: Coincident(g5,g6)
    c: Coincident(g6,g7)
    c: Coincident(g7,g4)
    c: Horizontal(g4)
    c: Horizontal(g6)
    c: Vertical(g5)
    c: Vertical(g7)
    c: DistanceY(g4) = -25
    c: Vertical(g8)
    c: Coincident(g8,g9)
    c: Horizontal(g9)
    c: Horizontal(g10)
    c: Coincident(g10,g11)
    c: Vertical(g11)
    c: Coincident(g11,g12)
    c: Coincident(g12,g13)
    c: Vertical(g13)
    c: Coincident(g13,g14)
    c: Coincident(g14,g15)
    c: Coincident(g15,g9)
    c: Coincident(g8,g10)
    c: Vertical(g15)
    c: DistanceY(g9) = -11
    c: DistanceY(g10) = -24
    c: Symmetric(g14,g13,g-2)
    c: Symmetric(g11,g12,g-2)
    c: DistanceX(g8) = -35
    c: Distance(g14) = 120
    c: DistanceY(g14) = 20
    c: DistanceY(g11) = -75
FEATURE [PartDesign::Body] Body
  Group = -> [Sketch,Pad,Sketch001,Pocket,Sketch003,Sketch004,Sketch007,Sketch008,Sketch009,Sketch010,Sketch017,Sketch019,Sketch021,Pocket002,Sketch022,Sketch024,Sketch025,Sketch026,Pocket003,Pocket004,Pocket005,Pocket006,Pocket007,Pocket008,Pad001,Pocket009,Pocket010,Sketch029,Sketch033,Sketch035,Sketch036,Sketch037,Pocket011,Pocket012,Pocket013,Pad002,Pocket014,Pad003,Sketch038,Sketch039,Pad004,Chamfer,+2 more]
  Origin = -> Origin
  Placement = pos=(0,0,0) rot=(0.862856,-0.357407,0.357407;1.71777rad)
  Tip = -> Chamfer001
